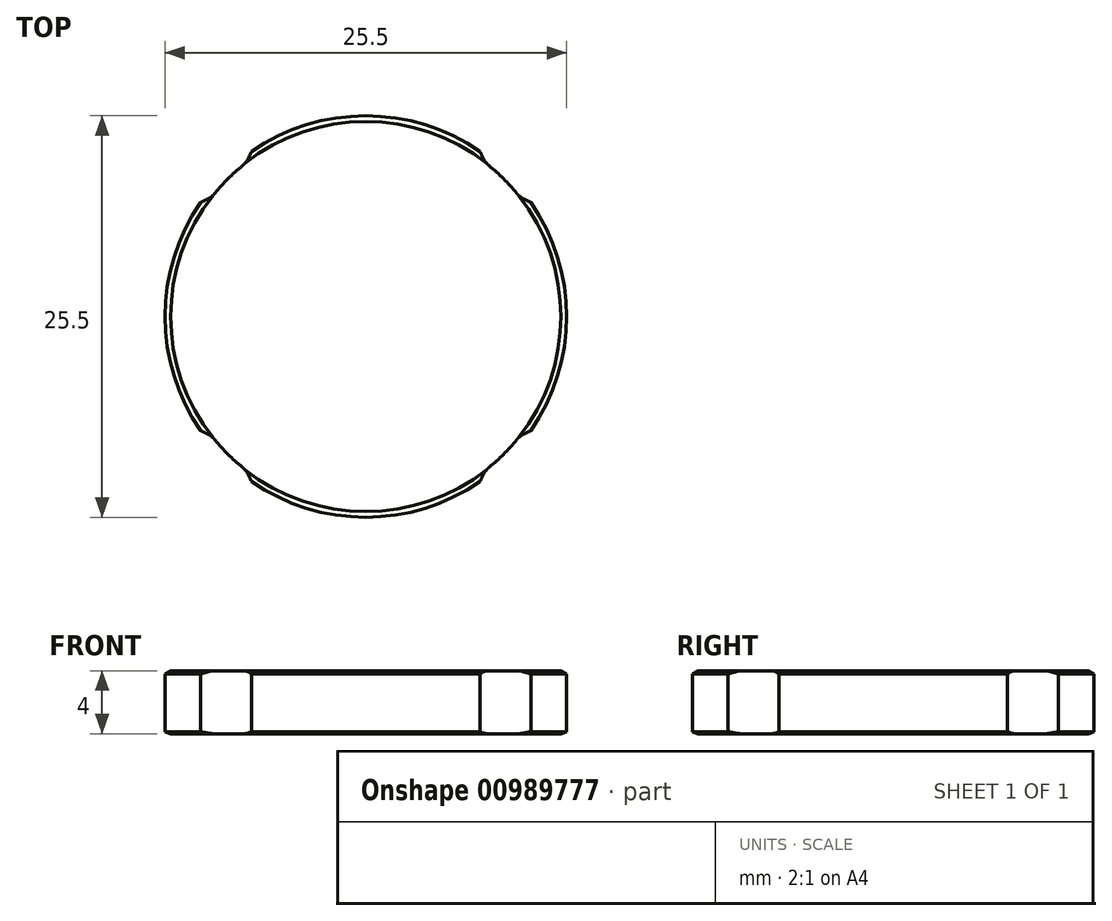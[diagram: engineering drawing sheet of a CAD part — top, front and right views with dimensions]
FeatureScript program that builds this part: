
annotation { "Feature Type Name" : "Feature", "Feature Type Description" : "" }
export const myFeature = defineFeature(function(context is Context, id is Id, definition is map)
    precondition{}
    {
        {
            var Q0;
            Q0=qCreatedBy(makeId("Top.planeOp"),FACE);
            var sketch = newSketch(context, id + "F0", { "sketchPlane" : qUnion([Q0])});
            skCircle(sketch, "E0", {"center": v(0, 0) * mm, "radius": 12.37 * mm});
            skCircle(sketch, "E1", {"center": v(0, 0) * mm, "radius": 12.75 * mm});
            skLineSegment(sketch, "E2", {"start": v(0, 0) * mm, "end": v(-18.44, 0) * mm, "construction": true});
            skLineSegment(sketch, "E3", {"start": v(-10.49, 0) * mm, "end": v(-10.49, -7.25) * mm, "construction": true});
            skLineSegment(sketch, "E4", {"start": v(-10.49, -7.25) * mm, "end": v(0, 0) * mm, "construction": true});
            skLineSegment(sketch, "E5", {"start": v(-10.49, -7.25) * mm, "end": v(-9.78, -7.59) * mm});
            skLineSegment(sketch, "E6.MirrorCS", {"start": v(-10.49, 7.25) * mm, "end": v(0, 0) * mm, "construction": true});
            skLineSegment(sketch, "E7.MirrorCS", {"start": v(-10.49, 0) * mm, "end": v(-10.49, 7.25) * mm, "construction": true});
            skLineSegment(sketch, "E8.MirrorCS", {"start": v(-10.49, 7.25) * mm, "end": v(-9.78, 7.59) * mm});
            skLineSegment(sketch, "E9.1.0", {"start": v(-7.25, -10.49) * mm, "end": v(-7.59, -9.78) * mm});
            skLineSegment(sketch, "E9.1.1", {"start": v(0, -10.49) * mm, "end": v(-7.25, -10.49) * mm, "construction": true});
            skLineSegment(sketch, "E9.1.2", {"start": v(-7.25, -10.49) * mm, "end": v(0, 0) * mm, "construction": true});
            skLineSegment(sketch, "E9.1.3", {"start": v(7.25, -10.49) * mm, "end": v(0, 0) * mm, "construction": true});
            skLineSegment(sketch, "E9.1.4", {"start": v(0, -10.49) * mm, "end": v(7.25, -10.49) * mm, "construction": true});
            skLineSegment(sketch, "E9.1.5", {"start": v(7.25, -10.49) * mm, "end": v(7.59, -9.78) * mm});
            skLineSegment(sketch, "E9.2.0", {"start": v(10.49, -7.25) * mm, "end": v(9.78, -7.59) * mm});
            skLineSegment(sketch, "E9.2.1", {"start": v(10.49, 0) * mm, "end": v(10.49, -7.25) * mm, "construction": true});
            skLineSegment(sketch, "E9.2.2", {"start": v(10.49, -7.25) * mm, "end": v(0, 0) * mm, "construction": true});
            skLineSegment(sketch, "E9.2.3", {"start": v(10.49, 7.25) * mm, "end": v(0, 0) * mm, "construction": true});
            skLineSegment(sketch, "E9.2.4", {"start": v(10.49, 0) * mm, "end": v(10.49, 7.25) * mm, "construction": true});
            skLineSegment(sketch, "E9.2.5", {"start": v(10.49, 7.25) * mm, "end": v(9.78, 7.59) * mm});
            skLineSegment(sketch, "E9.3.0", {"start": v(7.25, 10.49) * mm, "end": v(7.59, 9.78) * mm});
            skLineSegment(sketch, "E9.3.1", {"start": v(0, 10.49) * mm, "end": v(7.25, 10.49) * mm, "construction": true});
            skLineSegment(sketch, "E9.3.2", {"start": v(7.25, 10.49) * mm, "end": v(0, 0) * mm, "construction": true});
            skLineSegment(sketch, "E9.3.3", {"start": v(-7.25, 10.49) * mm, "end": v(0, 0) * mm, "construction": true});
            skLineSegment(sketch, "E9.3.4", {"start": v(0, 10.49) * mm, "end": v(-7.25, 10.49) * mm, "construction": true});
            skLineSegment(sketch, "E9.3.5", {"start": v(-7.25, 10.49) * mm, "end": v(-7.59, 9.78) * mm});
            skSolve(sketch);
        }
        {
            var Q0;
            {var subQ0=sQuery(id+"F0.wireOp",EDGE,"E9.3.0");Q0=makeQuery(id+"F0.imprint","IMPRINT",FACE,{"disambiguationData":[TD([[makeQuery(id+"F0.imprint","IMPRINT",EDGE,{"derivedFrom":subQ0}),-1.0]])]});}
            var Q1;
            {var subQ0=sQuery(id+"F0.wireOp",EDGE,"E5");Q1=makeQuery(id+"F0.imprint","IMPRINT",FACE,{"disambiguationData":[TD([[makeQuery(id+"F0.imprint","IMPRINT",EDGE,{"derivedFrom":subQ0}),1.0]])]});}
            var Q2;
            {var subQ0=sQuery(id+"F0.wireOp",EDGE,"E9.2.0");Q2=makeQuery(id+"F0.imprint","IMPRINT",FACE,{"disambiguationData":[TD([[makeQuery(id+"F0.imprint","IMPRINT",EDGE,{"derivedFrom":subQ0}),-1.0]])]});}
            var Q3;
            {var subQ0=sQuery(id+"F0.wireOp",EDGE,"E9.1.0");Q3=makeQuery(id+"F0.imprint","IMPRINT",FACE,{"disambiguationData":[TD([[makeQuery(id+"F0.imprint","IMPRINT",EDGE,{"derivedFrom":subQ0}),-1.0]])]});}
            var Q4;
            {var subQ0=sQuery(id+"F0.wireOp",EDGE,"E0");var subQ5=makeQuery(id+"F0.imprint","INTERSECT",VERTEX,{"derivedFrom":[subQ0,sQuery(id+"F0.wireOp",EDGE,"E9.2.5")]});Q4=makeQuery(id+"F0.imprint","IMPRINT",FACE,{"disambiguationData":[TD([[makeQuery(id+"F0.imprint","IMPRINT",EDGE,{"disambiguationData":[TD([[subQ5,-1.0]])],"derivedFrom":subQ0}),1.0]])]});}
            extrude(context, id + "F1", {"entities" : qUnion([Q0, Q1, Q2, Q3, Q4]), "depth" : 4 * mm, "offsetDistance" : 25 * mm});
        }
        {
            var Q0;
            {var subQ0=sQuery(id+"F0.wireOp",EDGE,"E1");Q0=makeQuery(id+"F1.opExtrude","CAP_EDGE",EDGE,{"disambiguationData":[OSD([subQ0]),TDD([makeQuery(id+"F0.imprint","IMPRINT",EDGE,{"disambiguationData":[TD([[makeQuery(id+"F0.imprint","INTERSECT",VERTEX,{"derivedFrom":[subQ0,sQuery(id+"F0.wireOp",EDGE,"E5")]}),1.0]])],"derivedFrom":subQ0})])],"isStart":false});}
            var Q1;
            {var subQ0=sQuery(id+"F0.wireOp",EDGE,"E1");Q1=makeQuery(id+"F1.opExtrude","CAP_EDGE",EDGE,{"disambiguationData":[OSD([subQ0]),TDD([makeQuery(id+"F0.imprint","IMPRINT",EDGE,{"disambiguationData":[TD([[makeQuery(id+"F0.imprint","INTERSECT",VERTEX,{"derivedFrom":[subQ0,sQuery(id+"F0.wireOp",EDGE,"E9.1.0")]}),-1.0]])],"derivedFrom":subQ0})])],"isStart":false});}
            var Q2;
            {var subQ0=sQuery(id+"F0.wireOp",EDGE,"E1");Q2=makeQuery(id+"F1.opExtrude","CAP_EDGE",EDGE,{"disambiguationData":[OSD([subQ0]),TDD([makeQuery(id+"F0.imprint","IMPRINT",EDGE,{"disambiguationData":[TD([[makeQuery(id+"F0.imprint","INTERSECT",VERTEX,{"derivedFrom":[subQ0,sQuery(id+"F0.wireOp",EDGE,"E9.2.0")]}),-1.0]])],"derivedFrom":subQ0})])],"isStart":false});}
            var Q3;
            {var subQ0=sQuery(id+"F0.wireOp",EDGE,"E1");Q3=makeQuery(id+"F1.opExtrude","CAP_EDGE",EDGE,{"disambiguationData":[OSD([subQ0]),TDD([makeQuery(id+"F0.imprint","IMPRINT",EDGE,{"disambiguationData":[TD([[makeQuery(id+"F0.imprint","INTERSECT",VERTEX,{"derivedFrom":[subQ0,sQuery(id+"F0.wireOp",EDGE,"E9.3.0")]}),-1.0]])],"derivedFrom":subQ0})])],"isStart":false});}
            chamfer(context, id + "F2", {"entities" : qUnion([Q0, Q1, Q2, Q3]), "chamferType" : ChamferType.OFFSET_ANGLE, "width" : .36 * mm, "oppositeDirection" : false, "angle" : 30 * degree, "tangentPropagation" : true});
        }
        {
            var Q0;
            {var subQ0=sQuery(id+"F0.wireOp",EDGE,"E1");Q0=makeQuery(id+"F1.opExtrude","CAP_EDGE",EDGE,{"disambiguationData":[OSD([subQ0]),TDD([makeQuery(id+"F0.imprint","IMPRINT",EDGE,{"disambiguationData":[TD([[makeQuery(id+"F0.imprint","INTERSECT",VERTEX,{"derivedFrom":[subQ0,sQuery(id+"F0.wireOp",EDGE,"E9.1.0")]}),-1.0]])],"derivedFrom":subQ0})])],"isStart":true});}
            var Q1;
            {var subQ0=sQuery(id+"F0.wireOp",EDGE,"E1");Q1=makeQuery(id+"F1.opExtrude","CAP_EDGE",EDGE,{"disambiguationData":[OSD([subQ0]),TDD([makeQuery(id+"F0.imprint","IMPRINT",EDGE,{"disambiguationData":[TD([[makeQuery(id+"F0.imprint","INTERSECT",VERTEX,{"derivedFrom":[subQ0,sQuery(id+"F0.wireOp",EDGE,"E9.2.0")]}),-1.0]])],"derivedFrom":subQ0})])],"isStart":true});}
            var Q2;
            {var subQ0=sQuery(id+"F0.wireOp",EDGE,"E1");Q2=makeQuery(id+"F1.opExtrude","CAP_EDGE",EDGE,{"disambiguationData":[OSD([subQ0]),TDD([makeQuery(id+"F0.imprint","IMPRINT",EDGE,{"disambiguationData":[TD([[makeQuery(id+"F0.imprint","INTERSECT",VERTEX,{"derivedFrom":[subQ0,sQuery(id+"F0.wireOp",EDGE,"E9.3.0")]}),-1.0]])],"derivedFrom":subQ0})])],"isStart":true});}
            var Q3;
            {var subQ0=sQuery(id+"F0.wireOp",EDGE,"E1");Q3=makeQuery(id+"F1.opExtrude","CAP_EDGE",EDGE,{"disambiguationData":[OSD([subQ0]),TDD([makeQuery(id+"F0.imprint","IMPRINT",EDGE,{"disambiguationData":[TD([[makeQuery(id+"F0.imprint","INTERSECT",VERTEX,{"derivedFrom":[subQ0,sQuery(id+"F0.wireOp",EDGE,"E5")]}),1.0]])],"derivedFrom":subQ0})])],"isStart":true});}
            chamfer(context, id + "F3", {"entities" : qUnion([Q0, Q1, Q2, Q3]), "chamferType" : ChamferType.OFFSET_ANGLE, "width" : .13 * mm, "oppositeDirection" : false, "angle" : 70 * degree, "tangentPropagation" : true});
        }
        {
            var Q0;
            Q0=makeQuery(id+"F1.opExtrude","SWEPT_EDGE",EDGE,{"disambiguationData":[OSD([sQuery(id+"F0.wireOp",EDGE,"E0"),sQuery(id+"F0.wireOp",EDGE,"E5")])]});
            var Q1;
            Q1=makeQuery(id+"F1.opExtrude","SWEPT_EDGE",EDGE,{"disambiguationData":[OSD([sQuery(id+"F0.wireOp",EDGE,"E0"),sQuery(id+"F0.wireOp",EDGE,"E9.1.0")])]});
            var Q2;
            Q2=makeQuery(id+"F1.opExtrude","SWEPT_EDGE",EDGE,{"disambiguationData":[OSD([sQuery(id+"F0.wireOp",EDGE,"E0"),sQuery(id+"F0.wireOp",EDGE,"E9.1.5")])]});
            var Q3;
            Q3=makeQuery(id+"F1.opExtrude","SWEPT_EDGE",EDGE,{"disambiguationData":[OSD([sQuery(id+"F0.wireOp",EDGE,"E0"),sQuery(id+"F0.wireOp",EDGE,"E9.2.0")])]});
            var Q4;
            Q4=makeQuery(id+"F1.opExtrude","SWEPT_EDGE",EDGE,{"disambiguationData":[OSD([sQuery(id+"F0.wireOp",EDGE,"E0"),sQuery(id+"F0.wireOp",EDGE,"E9.2.5")])]});
            var Q5;
            Q5=makeQuery(id+"F1.opExtrude","SWEPT_EDGE",EDGE,{"disambiguationData":[OSD([sQuery(id+"F0.wireOp",EDGE,"E0"),sQuery(id+"F0.wireOp",EDGE,"E9.3.0")])]});
            var Q6;
            Q6=makeQuery(id+"F1.opExtrude","SWEPT_EDGE",EDGE,{"disambiguationData":[OSD([sQuery(id+"F0.wireOp",EDGE,"E0"),sQuery(id+"F0.wireOp",EDGE,"E9.3.5")])]});
            var Q7;
            Q7=makeQuery(id+"F1.opExtrude","SWEPT_EDGE",EDGE,{"disambiguationData":[OSD([sQuery(id+"F0.wireOp",EDGE,"E0"),sQuery(id+"F0.wireOp",EDGE,"E8.MirrorCS")])]});
            fillet(context, id + "F4", {"entities" : qUnion([Q0, Q1, Q2, Q3, Q4, Q5, Q6, Q7]), "radius" : 1.5 * mm, "tangentPropagation" : true, "allowEdgeOverflow" : false});
        }
    });
